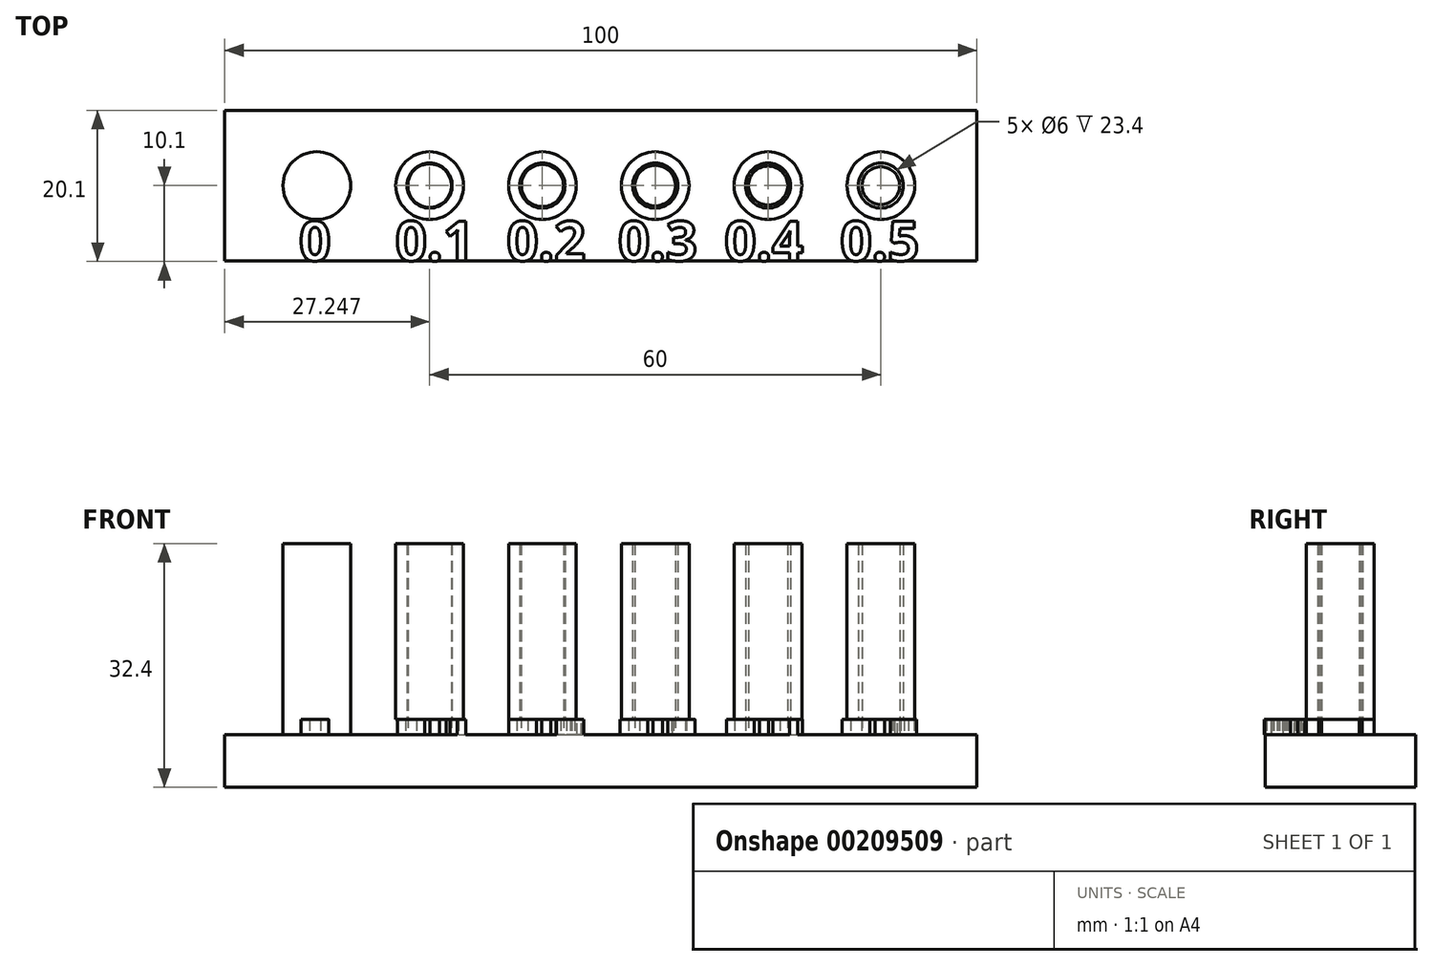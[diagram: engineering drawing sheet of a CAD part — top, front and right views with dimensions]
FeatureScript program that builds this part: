
annotation { "Feature Type Name" : "Feature", "Feature Type Description" : "" }
export const myFeature = defineFeature(function(context is Context, id is Id, definition is map)
    precondition{}
    {
        {
            var Q0;
            Q0=qCreatedBy(makeId("Top.planeOp"),FACE);
            var sketch = newSketch(context, id + "F0", { "sketchPlane" : qUnion([Q0])});
            skLineSegment(sketch, "E0.bottom", {"start": v(50, -10) * mm, "end": v(-50, -10) * mm});
            skLineSegment(sketch, "E0.top", {"start": v(50, 10) * mm, "end": v(-50, 10) * mm});
            skLineSegment(sketch, "E0.left", {"start": v(50, -10) * mm, "end": v(50, 10) * mm});
            skLineSegment(sketch, "E0.right", {"start": v(-50, -10) * mm, "end": v(-50, 10) * mm});
            skPoint(sketch, "E0.middle", {"position": v(0, 0) * mm});
            skSolve(sketch);
        }
        {
            var Q0;
            Q0 = qSketchRegion(id + "F0", true);
            extrude(context, id + "F1", {"entities" : qUnion([Q0]), "depth" : 7 * mm});
        }
        {
            var Q0;
            Q0=makeQuery(id+"F1.opExtrude","CAP_FACE",FACE,{"disambiguationData":[OSD([sQuery(id+"F0.wireOp",EDGE,"E0.bottom"),sQuery(id+"F0.wireOp",EDGE,"E0.top"),sQuery(id+"F0.wireOp",EDGE,"E0.left"),sQuery(id+"F0.wireOp",EDGE,"E0.right")])],"isStart":false});
            var sketch = newSketch(context, id + "F2", { "sketchPlane" : qUnion([Q0])});
            skCircle(sketch, "E1", {"center": v(-37.75, 0) * mm, "radius": 3 * mm});
            skCircle(sketch, "E2", {"center": v(-37.75, 0) * mm, "radius": 4.5 * mm});
            skCircle(sketch, "E3.1.0.0", {"center": v(-22.75, 0) * mm, "radius": 4.5 * mm});
            skCircle(sketch, "E3.1.0.1", {"center": v(-22.75, 0) * mm, "radius": 3 * mm});
            skCircle(sketch, "E3.2.0.0", {"center": v(-7.75, 0) * mm, "radius": 4.5 * mm});
            skCircle(sketch, "E3.2.0.1", {"center": v(-7.75, 0) * mm, "radius": 3 * mm});
            skCircle(sketch, "E3.3.0.0", {"center": v(7.25, 0) * mm, "radius": 4.5 * mm});
            skCircle(sketch, "E3.3.0.1", {"center": v(7.25, 0) * mm, "radius": 3 * mm});
            skCircle(sketch, "E3.4.0.0", {"center": v(22.25, 0) * mm, "radius": 4.5 * mm});
            skCircle(sketch, "E3.4.0.1", {"center": v(22.25, 0) * mm, "radius": 3 * mm});
            skCircle(sketch, "E3.5.0.0", {"center": v(37.25, 0) * mm, "radius": 4.5 * mm});
            skCircle(sketch, "E3.5.0.1", {"center": v(37.25, 0) * mm, "radius": 3 * mm});
            skLineSegment(sketch, "E3.direction1", {"start": v(-37.75, 0) * mm, "end": v(-22.75, 0) * mm, "construction": true});
            skCircle(sketch, "E4", {"center": v(-22.75, 0) * mm, "radius": 2.9 * mm});
            skCircle(sketch, "E5", {"center": v(-7.75, 0) * mm, "radius": 2.8 * mm});
            skCircle(sketch, "E6", {"center": v(7.25, 0) * mm, "radius": 2.7 * mm});
            skCircle(sketch, "E7", {"center": v(22.25, 0) * mm, "radius": 2.6 * mm});
            skCircle(sketch, "E8", {"center": v(37.25, 0) * mm, "radius": 2.5 * mm});
            skSolve(sketch);
        }
        {
            var Q0;
            Q0 = qSketchRegion(id + "F2", true);
            var Q1;
            Q1=makeQuery(id+"F2.imprint","IMPRINT",FACE,{"disambiguationData":[TD([[makeQuery(id+"F2.imprint","IMPRINT",EDGE,{"derivedFrom":sQuery(id+"F2.wireOp",EDGE,"E8")}),1.0]])]});
            var Q2;
            Q2=makeQuery(id+"F2.imprint","IMPRINT",FACE,{"disambiguationData":[TD([[makeQuery(id+"F2.imprint","IMPRINT",EDGE,{"derivedFrom":sQuery(id+"F2.wireOp",EDGE,"E7")}),1.0]])]});
            var Q3;
            Q3=makeQuery(id+"F2.imprint","IMPRINT",FACE,{"disambiguationData":[TD([[makeQuery(id+"F2.imprint","IMPRINT",EDGE,{"derivedFrom":sQuery(id+"F2.wireOp",EDGE,"E6")}),1.0]])]});
            var Q4;
            Q4=makeQuery(id+"F2.imprint","IMPRINT",FACE,{"disambiguationData":[TD([[makeQuery(id+"F2.imprint","IMPRINT",EDGE,{"derivedFrom":sQuery(id+"F2.wireOp",EDGE,"E5")}),1.0]])]});
            var Q5;
            Q5=makeQuery(id+"F2.imprint","IMPRINT",FACE,{"disambiguationData":[TD([[makeQuery(id+"F2.imprint","IMPRINT",EDGE,{"derivedFrom":sQuery(id+"F2.wireOp",EDGE,"E4")}),1.0]])]});
            var Q6;
            Q6=makeQuery(id+"F2.imprint","IMPRINT",FACE,{"disambiguationData":[TD([[makeQuery(id+"F2.imprint","IMPRINT",EDGE,{"derivedFrom":sQuery(id+"F2.wireOp",EDGE,"E1")}),1.0]])]});
            extrude(context, id + "F3", {"entities" : qUnion([Q0, Q1, Q2, Q3, Q4, Q5, Q6]), "operationType" : NewBodyOperationType.ADD, "depth" : 25.4 * mm});
        }
        {
            var Q0;
            {var subQ0=sQuery(id+"F0.wireOp",EDGE,"E0.right");var subQ1=sQuery(id+"F0.wireOp",EDGE,"E0.left");var subQ2=sQuery(id+"F0.wireOp",EDGE,"E0.top");var subQ3=sQuery(id+"F0.wireOp",EDGE,"E0.bottom");Q0=makeQuery(id+"F3.boolean.opBoolean","SPLIT",FACE,{"disambiguationData":[TD([makeQuery(id+"F1.opExtrude","SWEPT_FACE",FACE,{"disambiguationData":[OSD([subQ3])]})])],"derivedFrom":makeQuery(id+"F1.opExtrude","CAP_FACE",FACE,{"disambiguationData":[OSD([subQ3,subQ2,subQ1,subQ0])],"isStart":false})});}
            var sketch = newSketch(context, id + "F4", { "sketchPlane" : qUnion([Q0])});
            skText(sketch, "E9", { "text": "0", "fontName": "OpenSans-Bold.ttf"});
            skText(sketch, "E10", { "text": "0.1", "fontName": "OpenSans-Bold.ttf"});
            skText(sketch, "E11", { "text": "0.2", "fontName": "OpenSans-Bold.ttf"});
            skText(sketch, "E12", { "text": "0.3", "fontName": "OpenSans-Bold.ttf"});
            skText(sketch, "E13", { "text": "0.4", "fontName": "OpenSans-Bold.ttf"});
            skText(sketch, "E14", { "text": "0.5", "fontName": "OpenSans-Bold.ttf"});
            const initialGuessF4  = {"E9": [-0.0401, -0.01, 1, 0, 0.0053], "E10": [-0.02731, -0.01, 1, 0, 0.0053], "E11": [-0.0125, -0.01, 1, 0, 0.0053], "E12": [0.00232, -0.01, 1, 0, 0.0053], "E13": [0.01646, -0.01, 1, 0, 0.0053], "E14": [0.03185, -0.01, 1, 0, 0.0053]};
            skSetInitialGuess(sketch, initialGuessF4);
            skSolve(sketch);
        }
        {
            var Q0;
            Q0 = qSketchRegion(id + "F4", true);
            extrude(context, id + "F5", {"entities" : qUnion([Q0]), "operationType" : NewBodyOperationType.ADD, "depth" : 2 * mm});
        }
        {
            var Q0;
            {var subQ87=sQuery(id+"F0.wireOp",EDGE,"E0.bottom");var subQ88=makeQuery(id+"F1.opExtrude","SWEPT_FACE",FACE,{"disambiguationData":[OSD([subQ87])]});var subQ132=sQuery(id+"F0.wireOp",EDGE,"E0.left");var subQ136=sQuery(id+"F0.wireOp",EDGE,"E0.right");var subQ140=sQuery(id+"F0.wireOp",EDGE,"E0.top");Q0=makeQuery(id+"F5.boolean.opBoolean","SPLIT",FACE,{"disambiguationData":[TD([subQ88])],"derivedFrom":makeQuery(id+"F3.boolean.opBoolean","SPLIT",FACE,{"disambiguationData":[TD([subQ88])],"derivedFrom":makeQuery(id+"F1.opExtrude","CAP_FACE",FACE,{"disambiguationData":[OSD([subQ87,subQ140,subQ132,subQ136])],"isStart":false})})});}
            var sketch = newSketch(context, id + "F6", { "sketchPlane" : qUnion([Q0])});
            skCircle(sketch, "E15", {"center": v(-22.75, 0) * mm, "radius": 4.72 * mm});
            skCircle(sketch, "E16", {"center": v(-22.75, 0) * mm, "radius": 2.95 * mm});
            skCircle(sketch, "E17", {"center": v(-7.75, 0) * mm, "radius": 4.9 * mm});
            skCircle(sketch, "E18", {"center": v(-7.75, 0) * mm, "radius": 2.93 * mm});
            skCircle(sketch, "E19", {"center": v(7.25, 0) * mm, "radius": 4.78 * mm});
            skCircle(sketch, "E20", {"center": v(7.25, 0) * mm, "radius": 2.89 * mm});
            skCircle(sketch, "E21", {"center": v(22.25, 0) * mm, "radius": 4.72 * mm});
            skCircle(sketch, "E22", {"center": v(22.25, 0) * mm, "radius": 2.79 * mm});
            skCircle(sketch, "E23", {"center": v(37.25, 0) * mm, "radius": 4.74 * mm});
            skCircle(sketch, "E24", {"center": v(37.25, 0) * mm, "radius": 2.77 * mm});
            skSolve(sketch);
        }
        {
            var Q0;
            Q0 = qSketchRegion(id + "F6", true);
            extrude(context, id + "F7", {"entities" : qUnion([Q0]), "operationType" : NewBodyOperationType.REMOVE, "depth" : 2 * mm});
        }
    });
